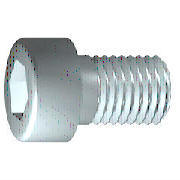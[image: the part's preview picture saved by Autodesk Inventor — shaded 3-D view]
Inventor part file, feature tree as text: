
AUTODESK INVENTOR PART (.ipt)
format: ipt  version: 2020 (Build 240168000, 168)  size: 198,144 bytes
history: native  units: mm (DEFAULTED — no unit token found)
features: sketch x2, other x1, extrude x1, plane x1, fillet x1
ambient origin geometry x7: Origin, YZ Plane, XY Plane, X Axis, Y Axis, Z Axis, Center Point
bodies: Solid1 (feature_tree)
feature tree (6):
  other  "Körper"
  extrude  "Loch"  Depth=2.0mm
  plane  "Work Plane1"
  fillet  "Fillet2"  Radius=2.0mm
  sketch  "Skizze1"  dims[d1=6.5mm d2=0.306825mm d3=2.0mm]
  sketch  "Skizze2"  dims[d4=1.5mm d5=60.0deg d6=3.0mm d7=3.0mm d8=2.309401mm d9=5.5mm d10=90.0deg d11=10.0mm d12=0.0mm d13=6.5mm d14=0.0mm d15=0.306725mm d16=0.306725mm d17=0.3mm d19=0.0mm d26=8.0mm d27=45.0deg d28=0.0mm d29=0.0mm d30=0.1mm]
